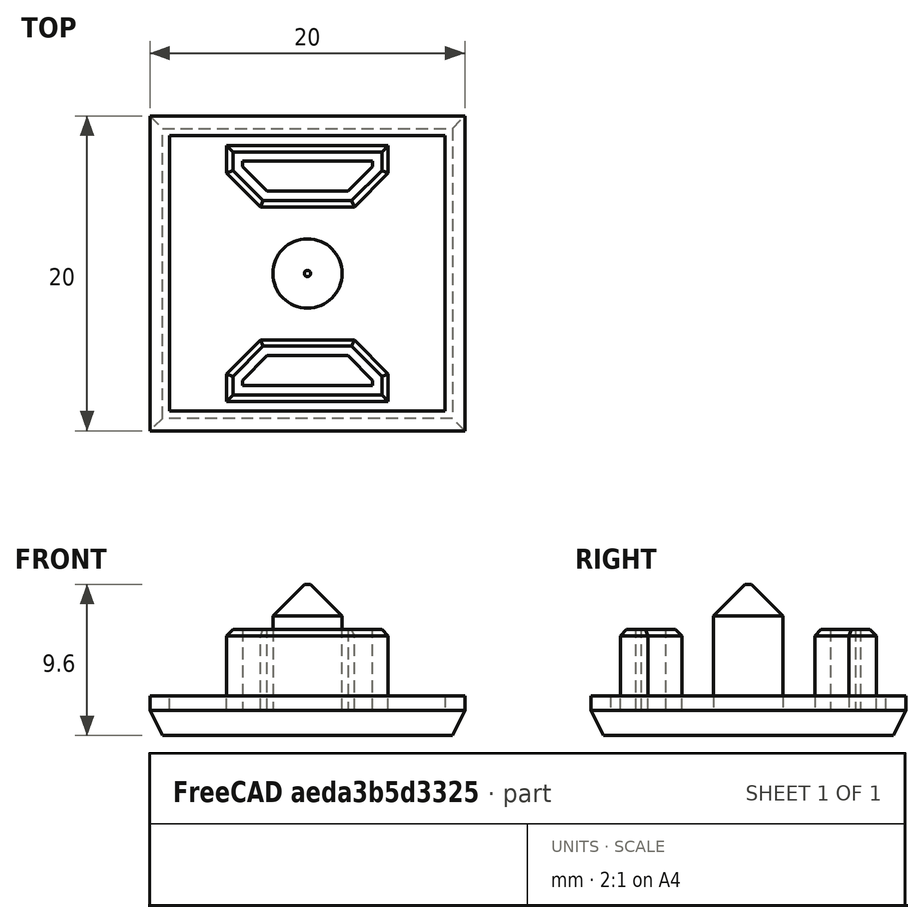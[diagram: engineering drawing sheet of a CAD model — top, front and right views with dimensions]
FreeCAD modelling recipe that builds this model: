
FCSTD DOCUMENT  (FreeCAD 1.1R44348 (Git))
Label: Ender32020Cap
License: All rights reserved
LicenseURL: https://en.wikipedia.org/wiki/All_rights_reserved
objects: Part::Feature×2, Sketcher::SketchObject×2, Mesh::Feature×1, Part::Refine×1, App::Point×1, PartDesign::FeatureBase×1, PartDesign::Pocket×1, PartDesign::Pad×1, PartDesign::Chamfer×1, PartDesign::Body×1
note: 19 computed .brp shape members not serialized (recipe doc carries the construction recipe); baked Part::Feature solids carry a one-line shape summary decoded from their .brp

FEATURE [Mesh::Feature] Ender_5_Extrusion_Cover_1_  label="Ender_5_Extrusion_Cover(1)"
FEATURE [Part::Feature] Ender_5_Extrusion_Cover_1_001
  shape: bbox 20 x 20 x 9.6 mm, 1296 faces, 0 solids (baked)
FEATURE [Part::Refine] Ender_5_Extrusion_Cover_1_002
  Source = -> Ender_5_Extrusion_Cover_1_001
FEATURE [Part::Feature] Ender_5_Extrusion_Cover_1_002_solid  label="Ender_5_Extrusion_Cover_1_002 (Solid)"
  shape: bbox 20 x 20 x 9.6 mm, 603 faces (baked)
FEATURE [App::Point] Origin001
  Role = Origin
FEATURE [PartDesign::FeatureBase] BaseFeature
  BaseFeature = -> Ender_5_Extrusion_Cover_1_002_solid
  Suppressed = false
FEATURE [Sketcher::SketchObject] Sketch
  ArcFitTolerance = 1e-06
  AttachmentSupport = -> [BaseFeature]
  ExternalTypes = [0]
  FullyConstrained = false
  MakeInternals = false
  MapMode = 5
  Placement = pos=(0,0,8) rot=(0,0,1;0rad)
  sketch-geometry (4):
    g0: LineSegment StartX=-3.01521 StartY=2.56095 StartZ=0 EndX=-3.01521 EndY=-2.72419 EndZ=0
    g1: LineSegment StartX=-3.01521 StartY=-2.72419 StartZ=0 EndX=3.11075 EndY=-2.72419 EndZ=0
    g2: LineSegment StartX=3.11075 StartY=-2.72419 StartZ=0 EndX=3.11075 EndY=2.56095 EndZ=0
    g3: LineSegment StartX=3.11075 StartY=2.56095 StartZ=0 EndX=-3.01521 EndY=2.56095 EndZ=0
  constraints (8):
    c: Coincident(g0,g1)
    c: Coincident(g1,g2)
    c: Coincident(g2,g3)
    c: Coincident(g3,g0)
    c: Vertical(g0)
    c: Vertical(g2)
    c: Horizontal(g1)
    c: Horizontal(g3)
FEATURE [PartDesign::Pocket] Pocket
  BaseFeature = -> BaseFeature
  Direction = (0,0,-1)
  Length = 5
  Length2 = 5
  Profile = -> Sketch
  ReferenceAxis = -> Sketch [N_Axis]
  Refine = true
  SideType = 0
  Suppressed = false
  Type = 3
  Type2 = 0
  UpToFace = -> BaseFeature [Face62]
FEATURE [Sketcher::SketchObject] Sketch001
  ArcFitTolerance = 1e-06
  AttachmentSupport = -> [Pocket]
  ExternalTypes = [0]
  FullyConstrained = true
  MakeInternals = false
  MapMode = 5
  sketch-geometry (1):
    g0: Circle CenterX=0 CenterY=0 CenterZ=0 NormalX=0 NormalY=0 NormalZ=1 AngleXU=0 Radius=2.2
  constraints (2):
    c: Coincident(g0,g-1)
    c: Diameter(g0) = 4.4
FEATURE [PartDesign::Pad] Pad
  BaseFeature = -> Pocket
  Direction = (0,0,1)
  Length = 8
  Length2 = 10
  Profile = -> Sketch001
  ReferenceAxis = -> Sketch001 [N_Axis]
  Refine = true
  SideType = 0
  Suppressed = false
  Type = 0
  Type2 = 0
FEATURE [PartDesign::Chamfer] Chamfer
  Angle = 45
  Base = -> Pad [Edge43]
  BaseFeature = -> Pad
  ChamferType = 0
  FlipDirection = false
  Refine = true
  Size = 2
  Size2 = 1
  SupportTransform = false
  Suppressed = false
  UseAllEdges = false
FEATURE [PartDesign::Body] Body
  AllowCompound = true
  BaseFeature = -> Ender_5_Extrusion_Cover_1_002_solid
  Group = -> [BaseFeature,Sketch,Pocket,Sketch001,Pad,Chamfer]
  Origin = -> Origin
  Tip = -> Chamfer
